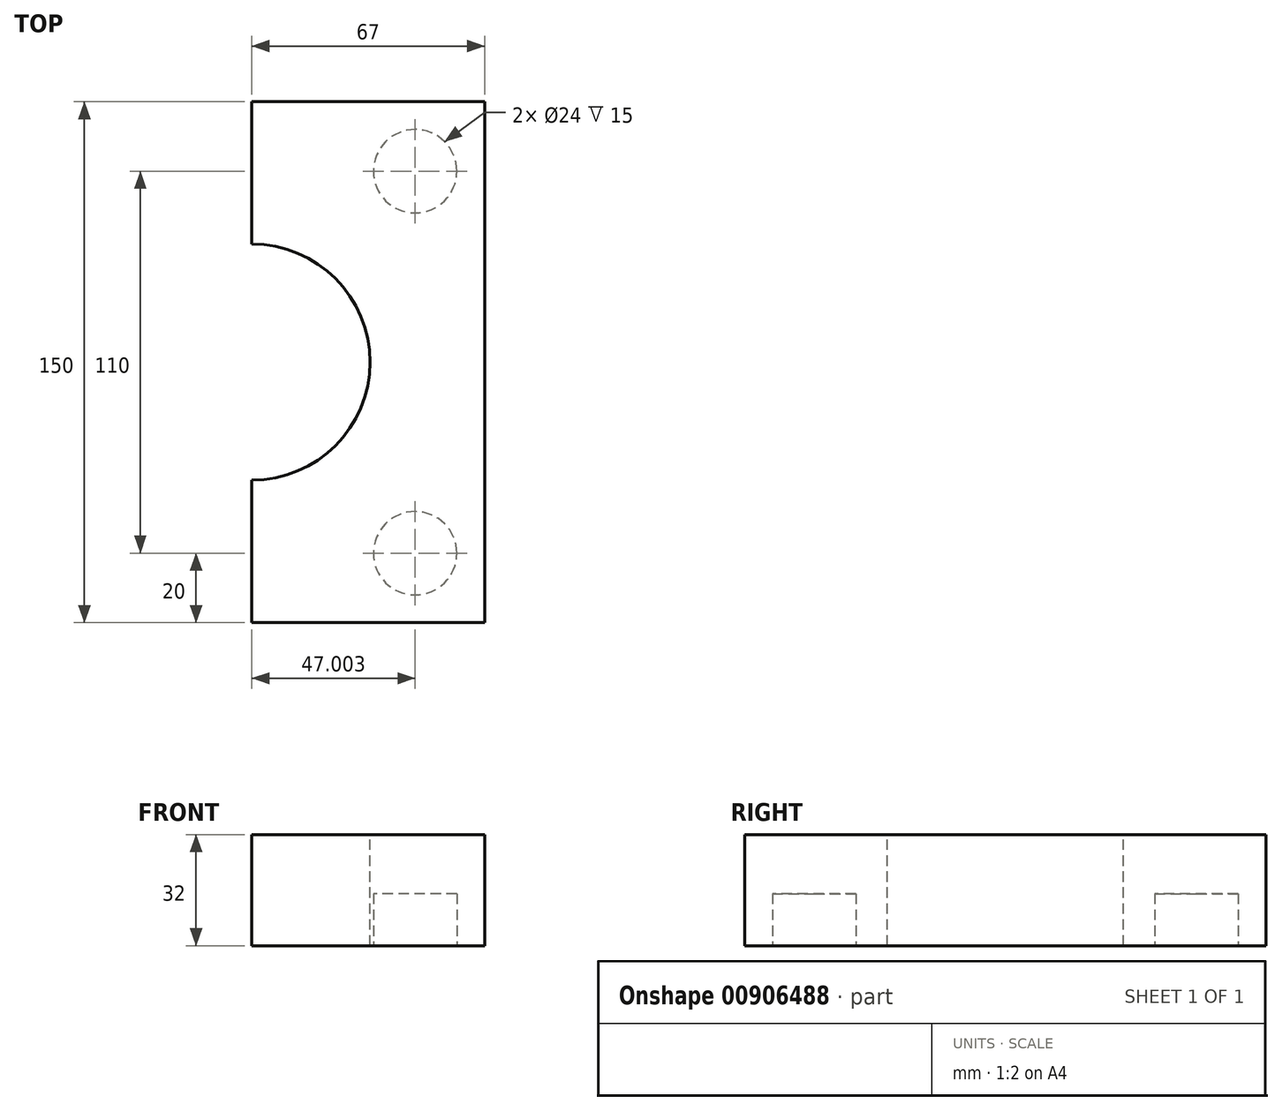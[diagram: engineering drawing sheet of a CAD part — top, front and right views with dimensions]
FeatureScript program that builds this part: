
annotation { "Feature Type Name" : "Feature", "Feature Type Description" : "" }
export const myFeature = defineFeature(function(context is Context, id is Id, definition is map)
    precondition{}
    {
        {
            var Q0;
            Q0=qCreatedBy(makeId("Top.planeOp"),FACE);
            var sketch = newSketch(context, id + "F0", { "sketchPlane" : qUnion([Q0])});
            skLineSegment(sketch, "E0.bottom", {"start": v(-4.76, 0) * mm, "end": v(-71.76, 0) * mm});
            skLineSegment(sketch, "E0.top", {"start": v(-4.76, -150) * mm, "end": v(-71.76, -150) * mm});
            skLineSegment(sketch, "E0.left", {"start": v(-4.76, 0) * mm, "end": v(-4.76, -150) * mm});
            skLineSegment(sketch, "E0.right", {"start": v(-71.76, 0) * mm, "end": v(-71.76, -150) * mm});
            skLineSegment(sketch, "E1.bottom", {"start": v(-71.76, 0) * mm, "end": v(-71.76, 0) * mm});
            skLineSegment(sketch, "E1.top", {"start": v(-71.76, -150) * mm, "end": v(-71.76, -150) * mm});
            skLineSegment(sketch, "E2.bottom", {"start": v(-71.76, 0) * mm, "end": v(-72.76, 0) * mm});
            skLineSegment(sketch, "E2.top", {"start": v(-71.76, -150) * mm, "end": v(-72.76, -150) * mm});
            skSolve(sketch);
        }
        {
            var Q0;
            {var subQ5=sQuery(id+"F0.wireOp",EDGE,"E0.bottom");Q0=makeQuery(id+"F0.imprint","IMPRINT",FACE,{"disambiguationData":[TD([[makeQuery(id+"F0.imprint","IMPRINT",EDGE,{"derivedFrom":subQ5}),1.0]])]});}
            var sketch = newSketch(context, id + "F1", { "sketchPlane" : qUnion([Q0])});
            skCircle(sketch, "E3", {"center": v(-24.76, -20) * mm, "radius": 12 * mm});
            skCircle(sketch, "E4", {"center": v(-24.76, -130) * mm, "radius": 12 * mm});
            skSolve(sketch);
        }
        {
            var Q0;
            Q0 = qSketchRegion(id + "F0", true);
            extrude(context, id + "F2", {"entities" : qUnion([Q0]), "depth" : 32 * mm, "offsetDistance" : 25 * mm});
        }
        {
            var Q0;
            Q0=makeQuery(id+"F2.opExtrude","CAP_FACE",FACE,{"disambiguationData":[OSD([sQuery(id+"F0.wireOp",EDGE,"E0.bottom"),sQuery(id+"F0.wireOp",EDGE,"E0.top"),sQuery(id+"F0.wireOp",EDGE,"E0.left"),sQuery(id+"F0.wireOp",EDGE,"E0.right")])],"isStart":false});
            var sketch = newSketch(context, id + "F3", { "sketchPlane" : qUnion([Q0])});
            skCircle(sketch, "E5", {"center": v(-71.76, -75) * mm, "radius": 34 * mm});
            skSolve(sketch);
        }
        {
            var Q0;
            Q0 = qSketchRegion(id + "F3", true);
            extrude(context, id + "F4", {"entities" : qUnion([Q0]), "operationType" : NewBodyOperationType.REMOVE, "oppositeDirection" : true, "depth" : 32 * mm, "offsetDistance" : 25 * mm});
        }
        {
            var Q0;
            Q0 = qSketchRegion(id + "F1", true);
            extrude(context, id + "F5", {"entities" : qUnion([Q0]), "operationType" : NewBodyOperationType.REMOVE, "depth" : 15 * mm, "offsetDistance" : 25 * mm});
        }
    });
